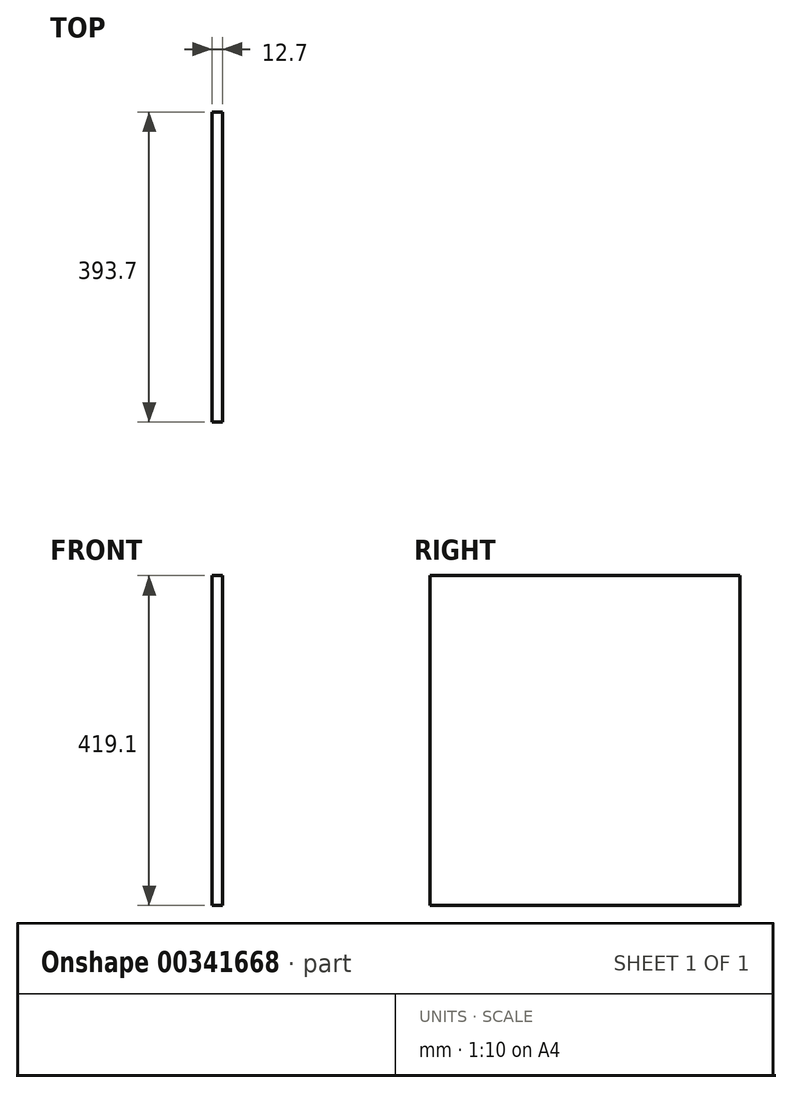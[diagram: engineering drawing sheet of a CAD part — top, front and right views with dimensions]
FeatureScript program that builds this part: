
annotation { "Feature Type Name" : "Feature", "Feature Type Description" : "" }
export const myFeature = defineFeature(function(context is Context, id is Id, definition is map)
    precondition{}
    {
        {
            var Q0;
            Q0=qCreatedBy(makeId("Right.planeOp"),FACE);
            var sketch = newSketch(context, id + "F0", { "sketchPlane" : qUnion([Q0])});
            skLineSegment(sketch, "E0.bottom", {"start": v(-189.57, 215.02) * mm, "end": v(204.13, 215.02) * mm});
            skLineSegment(sketch, "E0.top", {"start": v(-189.57, -204.08) * mm, "end": v(204.13, -204.08) * mm});
            skLineSegment(sketch, "E0.left", {"start": v(-189.57, 215.02) * mm, "end": v(-189.57, -204.08) * mm});
            skLineSegment(sketch, "E0.right", {"start": v(204.13, 215.02) * mm, "end": v(204.13, -204.08) * mm});
            skSolve(sketch);
        }
        {
            var Q0;
            Q0=makeQuery(id+"F0.imprint","IMPRINT",FACE,{"disambiguationData":[TD([[makeQuery(id+"F0.imprint","IMPRINT",EDGE,{"derivedFrom":sQuery(id+"F0.wireOp",EDGE,"E0.bottom")}),-1.0]])]});
            extrude(context, id + "F1", {"entities" : qUnion([Q0]), "depth" : 12.7 * mm, "offsetDistance" : 25.4 * mm});
        }
    });
